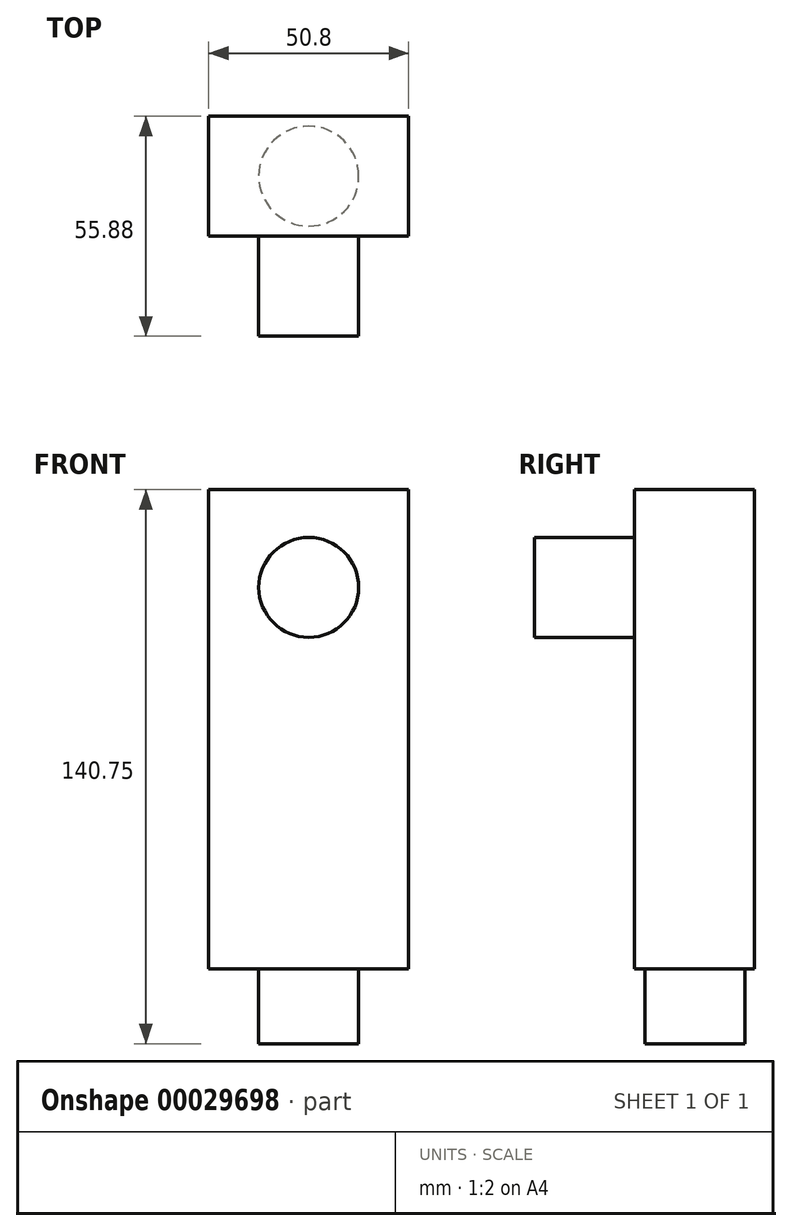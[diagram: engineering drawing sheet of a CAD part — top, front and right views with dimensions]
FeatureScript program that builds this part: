
annotation { "Feature Type Name" : "Feature", "Feature Type Description" : "" }
export const myFeature = defineFeature(function(context is Context, id is Id, definition is map)
    precondition{}
    {
        {
            var Q0;
            Q0=qCreatedBy(makeId("Front.planeOp"),FACE);
            var sketch = newSketch(context, id + "F0", { "sketchPlane" : qUnion([Q0])});
            skLineSegment(sketch, "E0.bottom", {"start": v(-25.4, 54.29) * mm, "end": v(25.4, 54.29) * mm});
            skLineSegment(sketch, "E0.top", {"start": v(-25.4, -67.4) * mm, "end": v(25.4, -67.4) * mm});
            skLineSegment(sketch, "E0.left", {"start": v(-25.4, 54.29) * mm, "end": v(-25.4, -67.4) * mm});
            skLineSegment(sketch, "E0.right", {"start": v(25.4, 54.29) * mm, "end": v(25.4, -67.4) * mm});
            skCircle(sketch, "E1", {"center": v(0, 29.47) * mm, "radius": 12.7 * mm});
            skSolve(sketch);
        }
        {
            var Q0;
            Q0 = qSketchRegion(id + "F0", true);
            var Q1;
            Q1=makeQuery(id+"F0.imprint","IMPRINT",FACE,{"disambiguationData":[TD([[makeQuery(id+"F0.imprint","IMPRINT",EDGE,{"derivedFrom":sQuery(id+"F0.wireOp",EDGE,"E0.bottom")}),-1.0]])]});
            extrude(context, id + "F1", {"entities" : qUnion([Q0, Q1]), "depth" : 30.48 * mm});
        }
        {
            var Q0;
            Q0=makeQuery(id+"F1.opExtrude","SWEPT_FACE",FACE,{"disambiguationData":[OSD([sQuery(id+"F0.wireOp",EDGE,"E0.top")])]});
            var sketch = newSketch(context, id + "F2", { "sketchPlane" : qUnion([Q0])});
            skCircle(sketch, "E2", {"center": v(0, 15.21) * mm, "radius": 12.7 * mm});
            skSolve(sketch);
        }
        {
            var Q0;
            Q0 = qSketchRegion(id + "F2", true);
            var Q1;
            Q1=makeQuery(id+"F2.imprint","IMPRINT",FACE,{"disambiguationData":[TD([[makeQuery(id+"F2.imprint","IMPRINT",EDGE,{"derivedFrom":sQuery(id+"F2.wireOp",EDGE,"E2")}),1.0]])]});
            extrude(context, id + "F3", {"entities" : qUnion([Q0, Q1]), "operationType" : NewBodyOperationType.ADD, "depth" : 19.05 * mm});
        }
        {
            var Q0;
            Q0=makeQuery(id+"F0.imprint","IMPRINT",FACE,{"disambiguationData":[TD([[makeQuery(id+"F0.imprint","IMPRINT",EDGE,{"derivedFrom":sQuery(id+"F0.wireOp",EDGE,"E1")}),1.0]])]});
            extrude(context, id + "F4", {"entities" : qUnion([Q0]), "operationType" : NewBodyOperationType.ADD, "depth" : 55.88 * mm});
        }
    });
